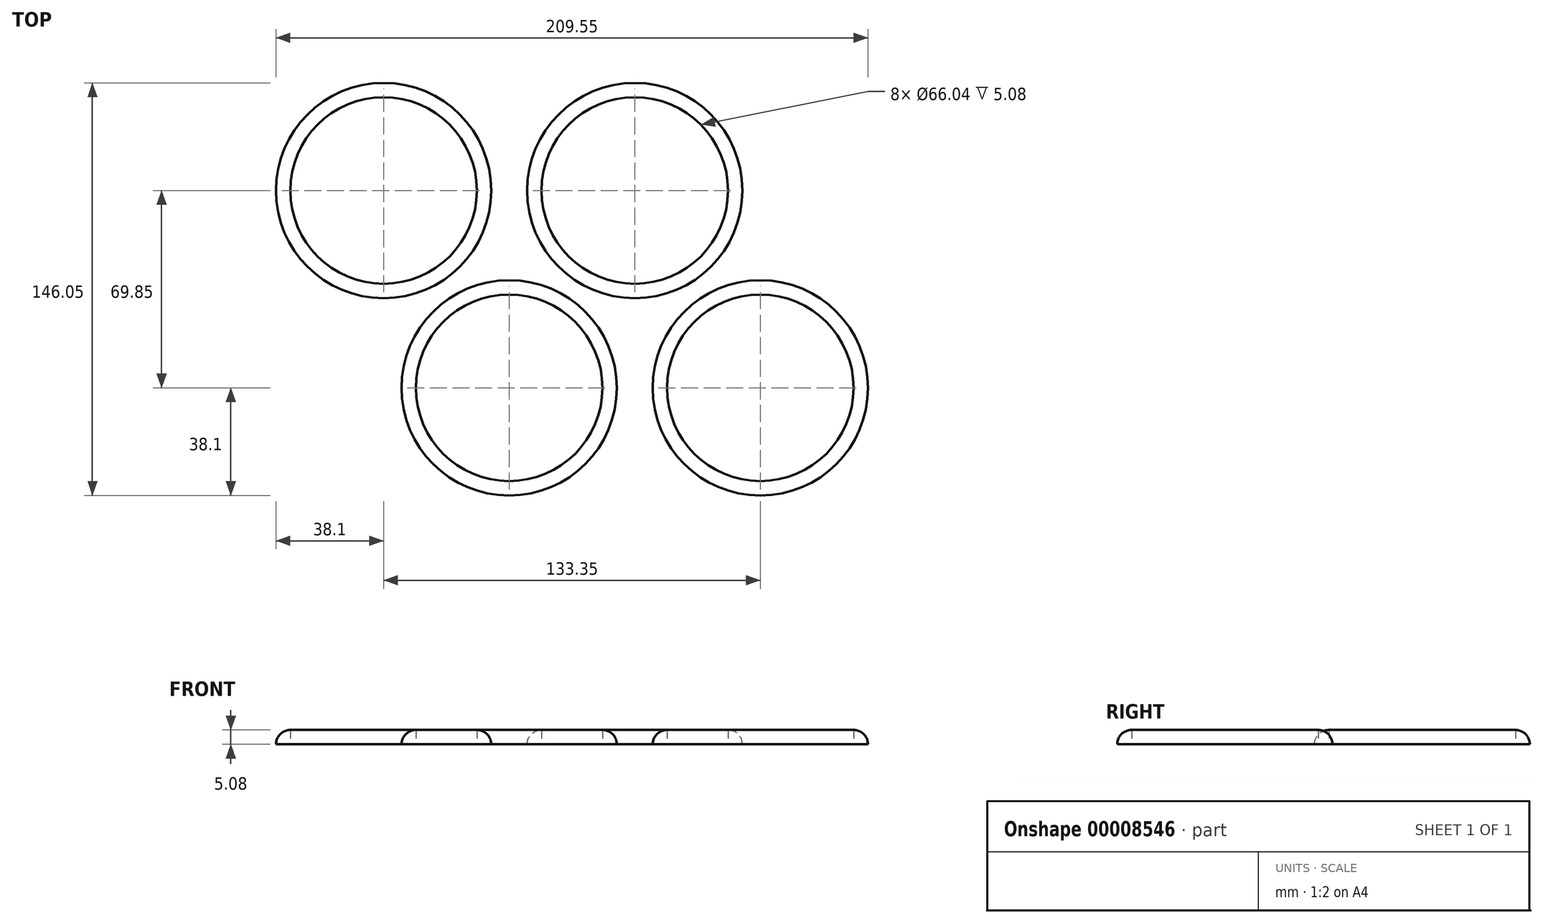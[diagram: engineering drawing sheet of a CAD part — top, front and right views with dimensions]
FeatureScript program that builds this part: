
annotation { "Feature Type Name" : "Feature", "Feature Type Description" : "" }
export const myFeature = defineFeature(function(context is Context, id is Id, definition is map)
    precondition{}
    {
        {
            var Q0;
            Q0=qCreatedBy(makeId("Top.planeOp"),FACE);
            var sketch = newSketch(context, id + "F0", { "sketchPlane" : qUnion([Q0])});
            skCircle(sketch, "E0", {"center": v(0, 0) * mm, "radius": 38.1 * mm});
            skCircle(sketch, "E1", {"center": v(0, 0) * mm, "radius": 33.02 * mm});
            skSolve(sketch);
        }
        {
            var Q0;
            Q0 = qSketchRegion(id + "F0", true);
            extrude(context, id + "F1", {"entities" : qUnion([Q0]), "depth" : 5.08 * mm});
        }
        {
            var Q0;
            Q0=makeQuery(id+"F1.opExtrude","SWEPT_BODY",BODY,{"disambiguationData":[OSD([sQuery(id+"F0.wireOp",EDGE,"E0"),sQuery(id+"F0.wireOp",EDGE,"E1")])]});
            transform(context, id + "F2", {"entities" : qUnion([Q0]), "transformType" : TransformType.TRANSLATION_3D, "dx" : 88.9 * mm, "dy" : 0 * mm, "dz" : 0 * mm, "makeCopy" : true});
        }
        {
            var Q0;
            Q0=makeQuery(id+"F1.opExtrude","CAP_EDGE",EDGE,{"disambiguationData":[OSD([sQuery(id+"F0.wireOp",EDGE,"E0")])],"isStart":false});
            var Q1;
            Q1=makeQuery(id+"F2.opPattern","COPY",EDGE,{"derivedFrom":makeQuery(id+"F1.opExtrude","CAP_EDGE",EDGE,{"disambiguationData":[OSD([sQuery(id+"F0.wireOp",EDGE,"E0")])],"isStart":false}),"instanceName":"1"});
            fillet(context, id + "F3", {"entities" : qUnion([Q0, Q1]), "radius" : 5.08 * mm, "tangentPropagation" : true, "allowEdgeOverflow" : false});
        }
        {
            var Q0;
            Q0=makeQuery(id+"F1.opExtrude","SWEPT_BODY",BODY,{"disambiguationData":[OSD([sQuery(id+"F0.wireOp",EDGE,"E0"),sQuery(id+"F0.wireOp",EDGE,"E1")])]});
            transform(context, id + "F4", {"entities" : qUnion([Q0]), "transformType" : TransformType.TRANSLATION_3D, "dx" : 44.45 * mm, "dy" : 69.85 * mm, "dz" : 0 * mm, "makeCopy" : true});
        }
        {
            var Q0;
            Q0=makeQuery(id+"F4.opPattern","COPY",BODY,{"derivedFrom":makeQuery(id+"F1.opExtrude","SWEPT_BODY",BODY,{"disambiguationData":[OSD([sQuery(id+"F0.wireOp",EDGE,"E0"),sQuery(id+"F0.wireOp",EDGE,"E1")])]}),"instanceName":"1"});
            transform(context, id + "F5", {"entities" : qUnion([Q0]), "transformType" : TransformType.TRANSLATION_3D, "dx" : -88.9 * mm, "dy" : 0 * mm, "dz" : 0 * mm, "makeCopy" : true});
        }
    });
